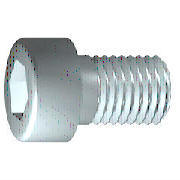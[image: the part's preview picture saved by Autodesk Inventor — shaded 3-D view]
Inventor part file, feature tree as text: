
AUTODESK INVENTOR PART (.ipt)
format: ipt  version: 2020 (Build 240168000, 168)  size: 188,928 bytes
history: native  units: mm (DEFAULTED — no unit token found)
features: sketch x2, other x1, extrude x1, plane x1, fillet x1
ambient origin geometry x7: Origin, YZ Plane, XY Plane, X Axis, Y Axis, Z Axis, Center Point
bodies: Solid1 (feature_tree)
feature tree (6):
  other  "Bryła"
  extrude  "Szczelina"  Depth=10.8mm
  plane  "Work Plane1"
  fillet  "Fillet2"  Radius=0.24548mm
  sketch  "Szkic1"
  sketch  "Szkic2"
